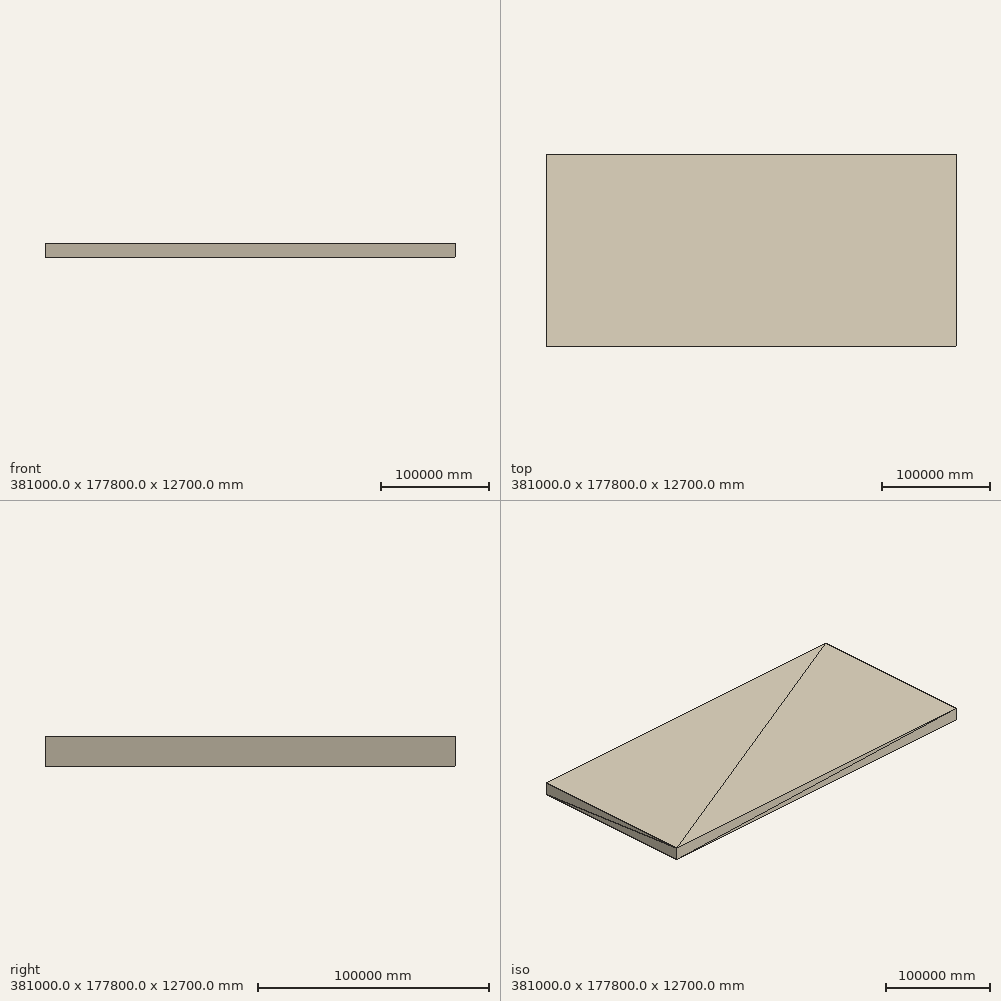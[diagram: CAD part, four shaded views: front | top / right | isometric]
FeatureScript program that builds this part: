
annotation { "Feature Type Name" : "Feature", "Feature Type Description" : "" }
export const myFeature = defineFeature(function(context is Context, id is Id, definition is map)
    precondition{}
    {
        {
            var Q0;
            Q0=qCreatedBy(makeId("Top.planeOp"),FACE);
            var sketch = newSketch(context, id + "F0", { "sketchPlane" : qUnion([Q0])});
            skLineSegment(sketch, "E0.bottom", {"start": v(0, 0) * mm, "end": v(381000, 0) * mm});
            skLineSegment(sketch, "E0.top", {"start": v(0, 177800) * mm, "end": v(381000, 177800) * mm});
            skLineSegment(sketch, "E0.left", {"start": v(0, 0) * mm, "end": v(0, 177800) * mm});
            skLineSegment(sketch, "E0.right", {"start": v(381000, 0) * mm, "end": v(381000, 177800) * mm});
            skSolve(sketch);
        }
        {
            var Q0;
            Q0 = qSketchRegion(id + "F0", true);
            extrude(context, id + "F1", {"entities" : qUnion([Q0]), "depth" : 12700 * mm, "offsetDistance" : 25.4 * mm});
        }
    });
